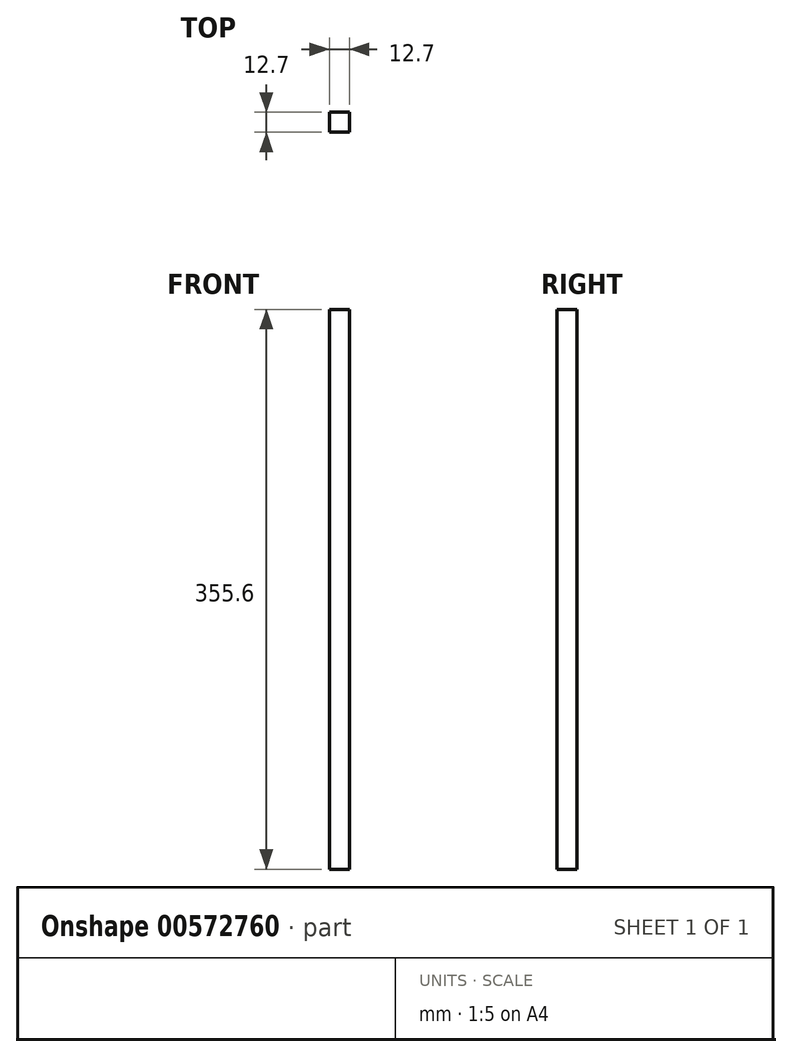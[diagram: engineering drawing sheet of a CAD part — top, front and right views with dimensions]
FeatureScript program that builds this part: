
annotation { "Feature Type Name" : "Feature", "Feature Type Description" : "" }
export const myFeature = defineFeature(function(context is Context, id is Id, definition is map)
    precondition{}
    {
        {
            var Q0;
            Q0=qCreatedBy(makeId("Right.planeOp"),FACE);
            var sketch = newSketch(context, id + "F0", { "sketchPlane" : qUnion([Q0])});
            skLineSegment(sketch, "E0.bottom", {"start": v(-6.35, 177.8) * mm, "end": v(6.35, 177.8) * mm});
            skLineSegment(sketch, "E0.top", {"start": v(-6.35, -177.8) * mm, "end": v(6.35, -177.8) * mm});
            skLineSegment(sketch, "E0.left", {"start": v(-6.35, 177.8) * mm, "end": v(-6.35, -177.8) * mm});
            skLineSegment(sketch, "E0.right", {"start": v(6.35, 177.8) * mm, "end": v(6.35, -177.8) * mm});
            skPoint(sketch, "E0.middle", {"position": v(0, 0) * mm});
            skSolve(sketch);
        }
        {
            var Q0;
            Q0 = qSketchRegion(id + "F0", true);
            extrude(context, id + "F1", {"entities" : qUnion([Q0]), "endBound" : BoundingType.SYMMETRIC, "depth" : 12.7 * mm, "offsetDistance" : 25.4 * mm});
        }
    });
